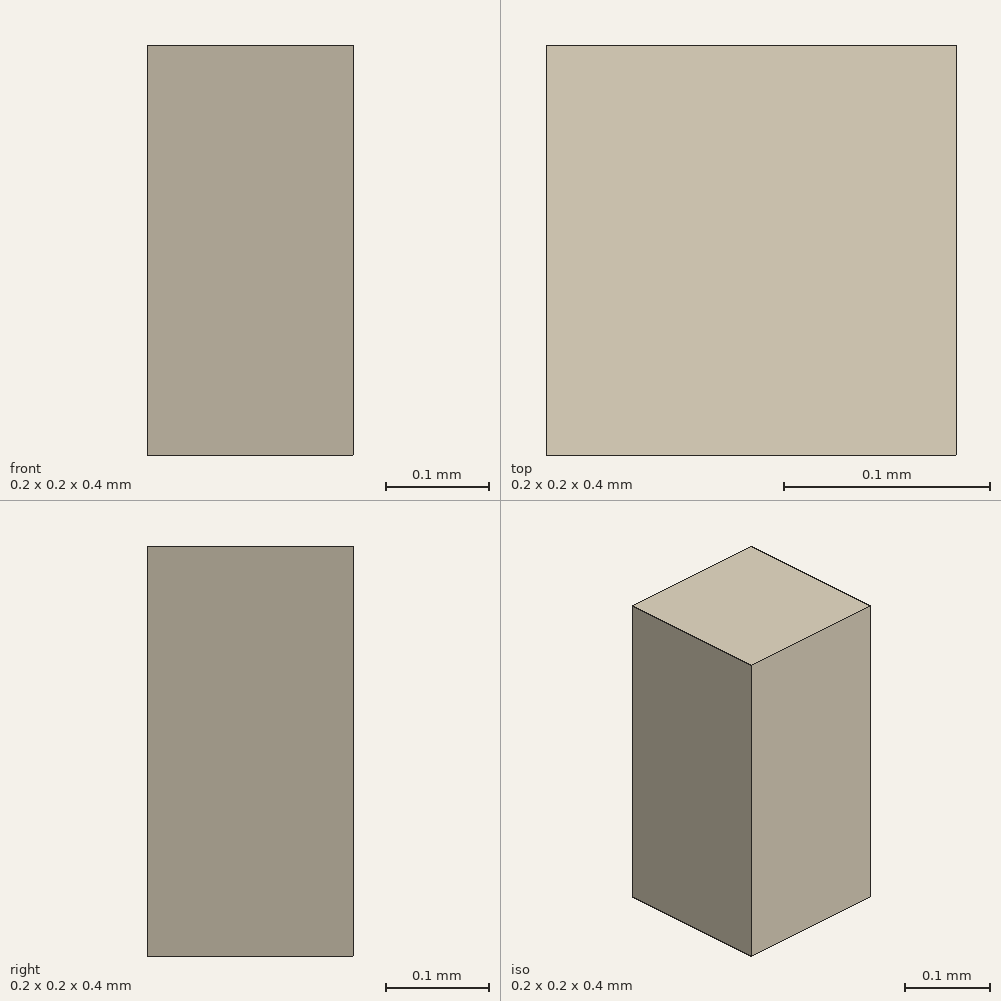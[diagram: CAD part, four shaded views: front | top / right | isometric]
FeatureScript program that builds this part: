
annotation { "Feature Type Name" : "Feature", "Feature Type Description" : "" }
export const myFeature = defineFeature(function(context is Context, id is Id, definition is map)
    precondition{}
    {
        {
            var Q0;
            Q0=qCreatedBy(makeId("Top.planeOp"),FACE);
            var sketch = newSketch(context, id + "F0", { "sketchPlane" : qUnion([Q0])});
            skLineSegment(sketch, "E0.bottom", {"start": v(17.41, 18.35) * mm, "end": v(17.21, 18.35) * mm});
            skLineSegment(sketch, "E0.top", {"start": v(17.41, 18.55) * mm, "end": v(17.21, 18.55) * mm});
            skLineSegment(sketch, "E0.left", {"start": v(17.41, 18.35) * mm, "end": v(17.41, 18.55) * mm});
            skLineSegment(sketch, "E0.right", {"start": v(17.21, 18.35) * mm, "end": v(17.21, 18.55) * mm});
            skPoint(sketch, "E0.middle", {"position": v(17.31, 18.45) * mm});
            skSolve(sketch);
        }
        {
            var Q0;
            Q0=makeQuery(id+"F0.imprint","IMPRINT",FACE,{"disambiguationData":[TD([[makeQuery(id+"F0.imprint","IMPRINT",EDGE,{"derivedFrom":sQuery(id+"F0.wireOp",EDGE,"E0.bottom")}),-1.0]])]});
            extrude(context, id + "F1", {"entities" : qUnion([Q0]), "depth" : 0.4 * mm});
        }
    });
